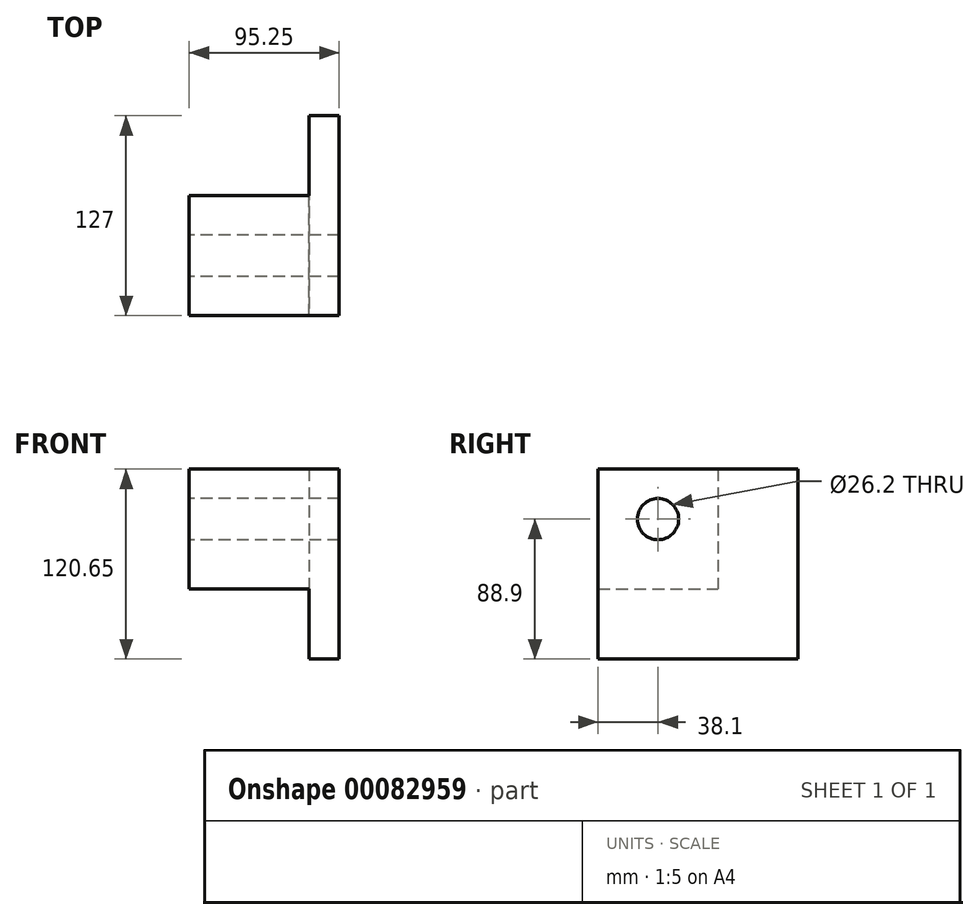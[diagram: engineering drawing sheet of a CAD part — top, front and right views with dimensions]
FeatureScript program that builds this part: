
annotation { "Feature Type Name" : "Feature", "Feature Type Description" : "" }
export const myFeature = defineFeature(function(context is Context, id is Id, definition is map)
    precondition{}
    {
        {
            var Q0;
            Q0=qCreatedBy(makeId("Front.planeOp"),FACE);
            var sketch = newSketch(context, id + "F0", { "sketchPlane" : qUnion([Q0])});
            skArc(sketch, "E0", {"start": v(0, 120.65) * mm, "mid": v(85.31, 85.31) * mm, "end": v(120.65, 0) * mm});
            skLineSegment(sketch, "E1", {"start": v(0, 0) * mm, "end": v(120.65, 0) * mm});
            skLineSegment(sketch, "E2", {"start": v(0, 0) * mm, "end": v(0, 120.65) * mm});
            skLineSegment(sketch, "E3.bottom", {"start": v(0, 120.65) * mm, "end": v(-19.05, 120.65) * mm});
            skLineSegment(sketch, "E3.top", {"start": v(0, 0) * mm, "end": v(-19.05, 0) * mm});
            skLineSegment(sketch, "E3.left", {"start": v(0, 120.65) * mm, "end": v(0, 0) * mm});
            skLineSegment(sketch, "E3.right", {"start": v(-19.05, 120.65) * mm, "end": v(-19.05, 0) * mm});
            skSolve(sketch);
        }
        {
            var Q0;
            Q0=makeQuery(id+"F0.imprint","IMPRINT",FACE,{"disambiguationData":[TD([[makeQuery(id+"F0.imprint","IMPRINT",EDGE,{"derivedFrom":sQuery(id+"F0.wireOp",EDGE,"E0")}),-1.0]])]});
            var Q1;
            Q1=makeQuery(id+"F0.imprint","IMPRINT",FACE,{"disambiguationData":[TD([[makeQuery(id+"F0.imprint","IMPRINT",EDGE,{"derivedFrom":sQuery(id+"F0.wireOp",EDGE,"E3.bottom")}),1.0]])]});
            extrude(context, id + "F1", {"entities" : qUnion([Q0, Q1]), "oppositeDirection" : true, "depth" : 127 * mm});
        }
        {
            var Q0;
            Q0=makeQuery(id+"F1.opExtrude","SWEPT_FACE",FACE,{"disambiguationData":[OSD([sQuery(id+"F0.wireOp",EDGE,"E3.right")])]});
            var sketch = newSketch(context, id + "F2", { "sketchPlane" : qUnion([Q0])});
            skLineSegment(sketch, "E4.bottom", {"start": v(0, 120.65) * mm, "end": v(-76.2, 120.65) * mm});
            skLineSegment(sketch, "E4.top", {"start": v(0, 44.45) * mm, "end": v(-76.2, 44.45) * mm});
            skLineSegment(sketch, "E4.left", {"start": v(0, 120.65) * mm, "end": v(0, 44.45) * mm});
            skLineSegment(sketch, "E4.right", {"start": v(-76.2, 120.65) * mm, "end": v(-76.2, 44.45) * mm});
            skSolve(sketch);
        }
        {
            var Q0;
            Q0 = qSketchRegion(id + "F2", true);
            extrude(context, id + "F3", {"entities" : qUnion([Q0]), "operationType" : NewBodyOperationType.ADD, "depth" : 76.2 * mm});
        }
        {
            var Q0;
            Q0=makeQuery(id+"F3.opExtrude","CAP_FACE",FACE,{"disambiguationData":[OSD([sQuery(id+"F2.wireOp",EDGE,"E4.bottom"),sQuery(id+"F2.wireOp",EDGE,"E4.top"),sQuery(id+"F2.wireOp",EDGE,"E4.left"),sQuery(id+"F2.wireOp",EDGE,"E4.right")])],"isStart":false});
            var sketch = newSketch(context, id + "F4", { "sketchPlane" : qUnion([Q0])});
            skLineSegment(sketch, "E5.bottom", {"start": v(0, 120.65) * mm, "end": v(-38.1, 120.65) * mm});
            skLineSegment(sketch, "E5.top", {"start": v(0, 88.9) * mm, "end": v(-38.1, 88.9) * mm});
            skLineSegment(sketch, "E5.left", {"start": v(0, 120.65) * mm, "end": v(0, 88.9) * mm});
            skLineSegment(sketch, "E5.right", {"start": v(-38.1, 120.65) * mm, "end": v(-38.1, 88.9) * mm});
            skCircle(sketch, "E6", {"center": v(-38.1, 88.9) * mm, "radius": 12.7 * mm});
            skSolve(sketch);
        }
        {
            var Q0;
            Q0=sQuery(id+"F4.wireOp",VERTEX,"E5.top.end");
            var Q1;
            Q1=makeQuery(id+"F1.opExtrude","SWEPT_BODY",BODY,{"disambiguationData":[OSD([sQuery(id+"F0.wireOp",EDGE,"E0"),sQuery(id+"F0.wireOp",EDGE,"E1"),sQuery(id+"F0.wireOp",EDGE,"E3.bottom"),sQuery(id+"F0.wireOp",EDGE,"E3.top"),sQuery(id+"F0.wireOp",EDGE,"E3.right")])]});
            hole(context, id + "F5", {"style" : HoleStyle.SIMPLE, "endStyle" : HoleEndStyle.THROUGH, "standardTappedOrClearance" : lookupTablePath({ "standard" : "ANSI", "fit" : "Normal (ASME)", "size" : "1", "type" : "Clearance" }), "standardBlindInLast" : lookupTablePath({ "fit" : "Free", "standard" : "ANSI", "size" : "1", "type" : "Clearance" }), "holeDiameter" : 26.2 * mm, "locations" : qUnion([Q0]), "scope" : qUnion([Q1]), "isTappedThrough" : true});
        }
        {
            var Q0;
            Q0=makeQuery(id+"F3.boolean.opBoolean","MERGE",FACE,{"derivedFrom":[makeQuery(id+"F1.opExtrude","CAP_FACE",FACE,{"disambiguationData":[OSD([sQuery(id+"F0.wireOp",EDGE,"E0"),sQuery(id+"F0.wireOp",EDGE,"E1"),sQuery(id+"F0.wireOp",EDGE,"E3.bottom"),sQuery(id+"F0.wireOp",EDGE,"E3.top"),sQuery(id+"F0.wireOp",EDGE,"E3.right")])],"isStart":true}),makeQuery(id+"F3.opExtrude","SWEPT_FACE",FACE,{"disambiguationData":[OSD([sQuery(id+"F2.wireOp",EDGE,"E4.left")])]})]});
            var sketch = newSketch(context, id + "F6", { "sketchPlane" : qUnion([Q0])});
            skLineSegment(sketch, "E7.bottom", {"start": v(120.65, 0) * mm, "end": v(57.15, 0) * mm});
            skLineSegment(sketch, "E7.top", {"start": v(120.65, 44.45) * mm, "end": v(57.15, 44.45) * mm});
            skLineSegment(sketch, "E7.left", {"start": v(120.65, 0) * mm, "end": v(120.65, 44.45) * mm});
            skLineSegment(sketch, "E7.right", {"start": v(57.15, 0) * mm, "end": v(57.15, 44.45) * mm});
            skCircle(sketch, "E8", {"center": v(57.15, 44.45) * mm, "radius": 12.7 * mm});
            skSolve(sketch);
        }
        {
            var Q0;
            Q0=sQuery(id+"F6.wireOp",VERTEX,"E7.top.end");
            var Q1;
            Q1=makeQuery(id+"F1.opExtrude","SWEPT_BODY",BODY,{"disambiguationData":[OSD([sQuery(id+"F0.wireOp",EDGE,"E0"),sQuery(id+"F0.wireOp",EDGE,"E1"),sQuery(id+"F0.wireOp",EDGE,"E3.bottom"),sQuery(id+"F0.wireOp",EDGE,"E3.top"),sQuery(id+"F0.wireOp",EDGE,"E3.right")])]});
            hole(context, id + "F7", {"style" : HoleStyle.SIMPLE, "endStyle" : HoleEndStyle.THROUGH, "holeDiameter" : 25.4 * mm, "locations" : qUnion([Q0]), "scope" : qUnion([Q1]), "isTappedThrough" : true});
        }
    });
